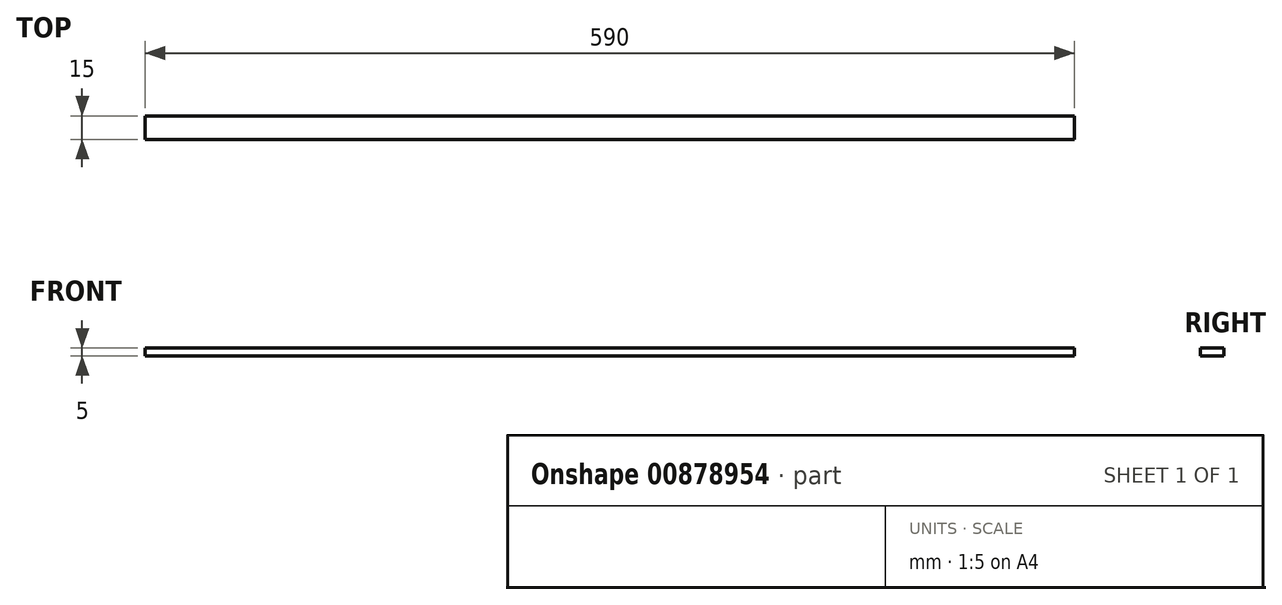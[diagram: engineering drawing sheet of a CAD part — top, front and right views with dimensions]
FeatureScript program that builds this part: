
annotation { "Feature Type Name" : "Feature", "Feature Type Description" : "" }
export const myFeature = defineFeature(function(context is Context, id is Id, definition is map)
    precondition{}
    {
        {
            var Q0;
            Q0=qCreatedBy(makeId("Top.planeOp"),FACE);
            var sketch = newSketch(context, id + "F0", { "sketchPlane" : qUnion([Q0])});
            skLineSegment(sketch, "E0.bottom", {"start": v(-18.5, 4.73) * mm, "end": v(571.5, 4.73) * mm});
            skLineSegment(sketch, "E0.top", {"start": v(-18.5, -10.27) * mm, "end": v(571.5, -10.27) * mm});
            skLineSegment(sketch, "E0.left", {"start": v(-18.5, 4.73) * mm, "end": v(-18.5, -10.27) * mm});
            skLineSegment(sketch, "E0.right", {"start": v(571.5, 4.73) * mm, "end": v(571.5, -10.27) * mm});
            skSolve(sketch);
        }
        {
            var Q0;
            Q0 = qSketchRegion(id + "F0", true);
            extrude(context, id + "F1", {"entities" : qUnion([Q0]), "depth" : 5 * mm, "offsetDistance" : 25 * mm});
        }
    });
